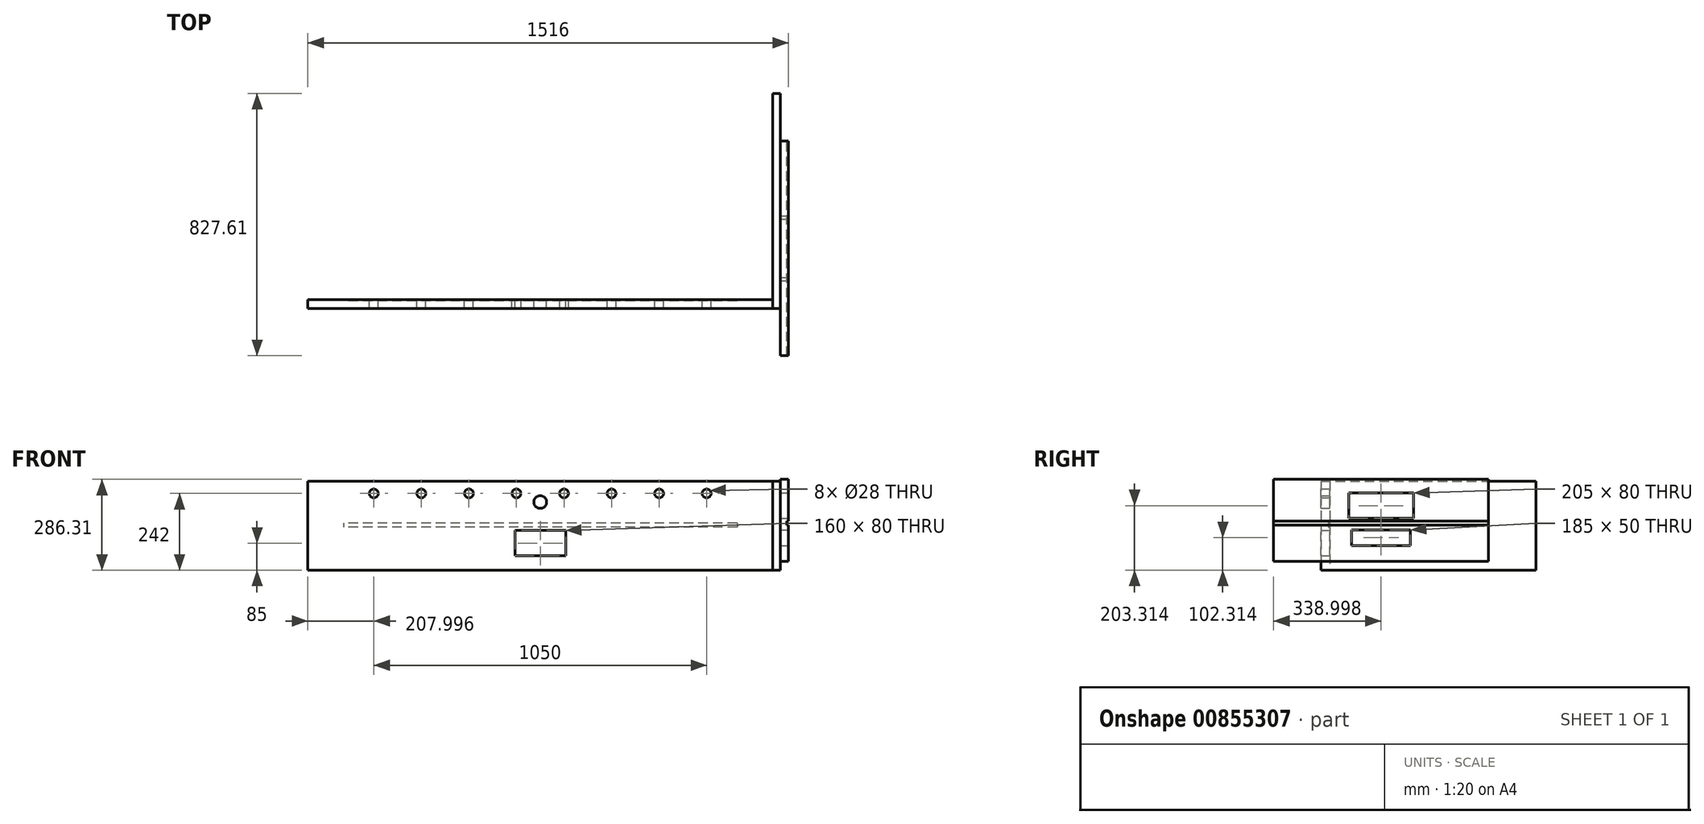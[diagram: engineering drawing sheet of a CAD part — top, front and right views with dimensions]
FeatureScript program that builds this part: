
annotation { "Feature Type Name" : "Feature", "Feature Type Description" : "" }
export const myFeature = defineFeature(function(context is Context, id is Id, definition is map)
    precondition{}
    {
        {
            var Q0;
            Q0=qCreatedBy(makeId("Front.planeOp"),FACE);
            var sketch = newSketch(context, id + "F0", { "sketchPlane" : qUnion([Q0])});
            skLineSegment(sketch, "E0.bottom", {"start": v(-1032.32, -125.07) * mm, "end": v(433.68, -125.07) * mm});
            skLineSegment(sketch, "E0.top", {"start": v(-1032.32, -405.07) * mm, "end": v(433.68, -405.07) * mm});
            skLineSegment(sketch, "E0.left", {"start": v(-1032.32, -125.07) * mm, "end": v(-1032.32, -405.07) * mm});
            skLineSegment(sketch, "E0.right", {"start": v(433.68, -125.07) * mm, "end": v(433.68, -405.07) * mm});
            skCircle(sketch, "E1", {"center": v(-824.32, -163.07) * mm, "radius": 14 * mm});
            skCircle(sketch, "E2", {"center": v(-524.32, -163.07) * mm, "radius": 14 * mm});
            skCircle(sketch, "E3", {"center": v(-374.32, -163.07) * mm, "radius": 14 * mm});
            skCircle(sketch, "E4", {"center": v(-224.32, -163.07) * mm, "radius": 14 * mm});
            skCircle(sketch, "E5", {"center": v(-74.32, -163.07) * mm, "radius": 14 * mm});
            skCircle(sketch, "E6", {"center": v(75.68, -163.07) * mm, "radius": 14 * mm});
            skCircle(sketch, "E7", {"center": v(225.68, -163.07) * mm, "radius": 14 * mm});
            skCircle(sketch, "E8", {"center": v(-674.32, -163.07) * mm, "radius": 14 * mm});
            skCircle(sketch, "E9", {"center": v(-299.32, -190.07) * mm, "radius": 20 * mm});
            skLineSegment(sketch, "E10.bottom", {"start": v(-219.32, -360.07) * mm, "end": v(-379.32, -360.07) * mm});
            skLineSegment(sketch, "E10.top", {"start": v(-219.32, -280.07) * mm, "end": v(-379.32, -280.07) * mm});
            skLineSegment(sketch, "E10.left", {"start": v(-219.32, -360.07) * mm, "end": v(-219.32, -280.07) * mm});
            skLineSegment(sketch, "E10.right", {"start": v(-379.32, -360.07) * mm, "end": v(-379.32, -280.07) * mm});
            skPoint(sketch, "E10.middle", {"position": v(-299.32, -320.07) * mm});
            skSolve(sketch);
        }
        {
            var Q0;
            Q0 = qSketchRegion(id + "F0", true);
            extrude(context, id + "F1", {"entities" : qUnion([Q0]), "depth" : 28 * mm, "offsetDistance" : 25 * mm});
        }
        {
            var Q0;
            Q0=makeQuery(id+"F1.opExtrude","SWEPT_FACE",FACE,{"disambiguationData":[OSD([sQuery(id+"F0.wireOp",EDGE,"E0.right")])]});
            var sketch = newSketch(context, id + "F2", { "sketchPlane" : qUnion([Q0])});
            skLineSegment(sketch, "E11.bottom", {"start": v(-28, -125.07) * mm, "end": v(650, -125.07) * mm});
            skLineSegment(sketch, "E11.top", {"start": v(-28, -405.07) * mm, "end": v(650, -405.07) * mm});
            skLineSegment(sketch, "E11.left", {"start": v(-28, -125.07) * mm, "end": v(-28, -405.07) * mm});
            skLineSegment(sketch, "E11.right", {"start": v(650, -125.07) * mm, "end": v(650, -405.07) * mm});
            skSolve(sketch);
        }
        {
            var Q0;
            Q0 = qSketchRegion(id + "F2", true);
            extrude(context, id + "F3", {"entities" : qUnion([Q0]), "depth" : 25 * mm, "offsetDistance" : 25 * mm});
        }
        {
            var Q0;
            Q0=makeQuery(id+"F1.opExtrude","CAP_FACE",FACE,{"disambiguationData":[OSD([sQuery(id+"F0.wireOp",EDGE,"E0.bottom"),sQuery(id+"F0.wireOp",EDGE,"E0.top"),sQuery(id+"F0.wireOp",EDGE,"E0.left"),sQuery(id+"F0.wireOp",EDGE,"E0.right"),sQuery(id+"F0.wireOp",EDGE,"E1"),sQuery(id+"F0.wireOp",EDGE,"E2"),sQuery(id+"F0.wireOp",EDGE,"E3"),sQuery(id+"F0.wireOp",EDGE,"E4"),sQuery(id+"F0.wireOp",EDGE,"E5"),sQuery(id+"F0.wireOp",EDGE,"E6"),sQuery(id+"F0.wireOp",EDGE,"E7"),sQuery(id+"F0.wireOp",EDGE,"E8"),sQuery(id+"F0.wireOp",EDGE,"E9"),sQuery(id+"F0.wireOp",EDGE,"E10.bottom"),sQuery(id+"F0.wireOp",EDGE,"E10.top"),sQuery(id+"F0.wireOp",EDGE,"E10.left"),sQuery(id+"F0.wireOp",EDGE,"E10.right")])],"isStart":true});
            var sketch = newSketch(context, id + "F4", { "sketchPlane" : qUnion([Q0])});
            skLineSegment(sketch, "E12.bottom", {"start": v(-321.68, -256.07) * mm, "end": v(920.32, -256.07) * mm});
            skLineSegment(sketch, "E12.top", {"start": v(-321.68, -269.07) * mm, "end": v(920.32, -269.07) * mm});
            skLineSegment(sketch, "E12.left", {"start": v(-321.68, -256.07) * mm, "end": v(-321.68, -269.07) * mm});
            skLineSegment(sketch, "E12.right", {"start": v(920.32, -256.07) * mm, "end": v(920.32, -269.07) * mm});
            skSolve(sketch);
        }
        {
            var Q0;
            Q0 = qSketchRegion(id + "F4", true);
            extrude(context, id + "F5", {"entities" : qUnion([Q0]), "operationType" : NewBodyOperationType.REMOVE, "oppositeDirection" : true, "depth" : 5 * mm, "offsetDistance" : 25 * mm});
        }
        {
            var Q0;
            Q0=makeQuery(id+"F3.opExtrude","CAP_FACE",FACE,{"disambiguationData":[OSD([sQuery(id+"F2.wireOp",EDGE,"E11.bottom"),sQuery(id+"F2.wireOp",EDGE,"E11.top"),sQuery(id+"F2.wireOp",EDGE,"E11.left"),sQuery(id+"F2.wireOp",EDGE,"E11.right")])],"isStart":false});
            var sketch = newSketch(context, id + "F6", { "sketchPlane" : qUnion([Q0])});
            skLineSegment(sketch, "E13.bottom", {"start": v(-177.61, -118.76) * mm, "end": v(500.39, -118.76) * mm});
            skLineSegment(sketch, "E13.top", {"start": v(-177.61, -376.76) * mm, "end": v(500.39, -376.76) * mm});
            skLineSegment(sketch, "E13.left", {"start": v(-177.61, -118.76) * mm, "end": v(-177.61, -376.76) * mm});
            skLineSegment(sketch, "E13.right", {"start": v(500.39, -118.76) * mm, "end": v(500.39, -376.76) * mm});
            skSolve(sketch);
        }
        {
            var Q0;
            Q0 = qSketchRegion(id + "F6", true);
            extrude(context, id + "F7", {"entities" : qUnion([Q0]), "depth" : 25 * mm, "offsetDistance" : 25 * mm});
        }
        {
            var Q0;
            Q0=makeQuery(id+"F7.opExtrude","CAP_FACE",FACE,{"disambiguationData":[OSD([sQuery(id+"F6.wireOp",EDGE,"E13.bottom"),sQuery(id+"F6.wireOp",EDGE,"E13.top"),sQuery(id+"F6.wireOp",EDGE,"E13.left"),sQuery(id+"F6.wireOp",EDGE,"E13.right")])],"isStart":false});
            var sketch = newSketch(context, id + "F8", { "sketchPlane" : qUnion([Q0])});
            skLineSegment(sketch, "E14.bottom", {"start": v(263.89, -161.76) * mm, "end": v(58.89, -161.76) * mm});
            skLineSegment(sketch, "E14.top", {"start": v(263.89, -241.76) * mm, "end": v(58.89, -241.76) * mm});
            skLineSegment(sketch, "E14.left", {"start": v(263.89, -161.76) * mm, "end": v(263.89, -241.76) * mm});
            skLineSegment(sketch, "E14.right", {"start": v(58.89, -161.76) * mm, "end": v(58.89, -241.76) * mm});
            skPoint(sketch, "E14.middle", {"position": v(161.39, -201.76) * mm});
            skLineSegment(sketch, "E15.bottom", {"start": v(253.89, -327.76) * mm, "end": v(68.89, -327.76) * mm});
            skLineSegment(sketch, "E15.top", {"start": v(253.89, -277.76) * mm, "end": v(68.89, -277.76) * mm});
            skLineSegment(sketch, "E15.left", {"start": v(253.89, -327.76) * mm, "end": v(253.89, -277.76) * mm});
            skLineSegment(sketch, "E15.right", {"start": v(68.89, -327.76) * mm, "end": v(68.89, -277.76) * mm});
            skPoint(sketch, "E15.middle", {"position": v(161.39, -302.76) * mm});
            skSolve(sketch);
        }
        {
            var Q0;
            Q0=makeQuery(id+"F8.imprint","IMPRINT",FACE,{"disambiguationData":[TD([[makeQuery(id+"F8.imprint","IMPRINT",EDGE,{"derivedFrom":sQuery(id+"F8.wireOp",EDGE,"E14.bottom")}),1.0]])]});
            var Q1;
            Q1=makeQuery(id+"F8.imprint","IMPRINT",FACE,{"disambiguationData":[TD([[makeQuery(id+"F8.imprint","IMPRINT",EDGE,{"derivedFrom":sQuery(id+"F8.wireOp",EDGE,"E15.bottom")}),-1.0]])]});
            var Q2;
            Q2=makeQuery(id+"F7.opExtrude","CAP_FACE",FACE,{"disambiguationData":[OSD([sQuery(id+"F6.wireOp",EDGE,"E13.bottom"),sQuery(id+"F6.wireOp",EDGE,"E13.top"),sQuery(id+"F6.wireOp",EDGE,"E13.left"),sQuery(id+"F6.wireOp",EDGE,"E13.right")])],"isStart":true});
            extrude(context, id + "F9", {"entities" : qUnion([Q0, Q1]), "operationType" : NewBodyOperationType.REMOVE, "endBound" : BoundingType.UP_TO_SURFACE, "oppositeDirection" : true, "depth" : 25 * mm, "endBoundEntityFace" : qUnion([Q2]), "offsetDistance" : 25 * mm});
        }
        {
            var Q0;
            Q0=makeQuery(id+"F7.opExtrude","CAP_FACE",FACE,{"disambiguationData":[OSD([sQuery(id+"F6.wireOp",EDGE,"E13.bottom"),sQuery(id+"F6.wireOp",EDGE,"E13.top"),sQuery(id+"F6.wireOp",EDGE,"E13.left"),sQuery(id+"F6.wireOp",EDGE,"E13.right")])],"isStart":false});
            var sketch = newSketch(context, id + "F10", { "sketchPlane" : qUnion([Q0])});
            skLineSegment(sketch, "E16.bottom", {"start": v(-189.61, -249.76) * mm, "end": v(510.39, -249.76) * mm});
            skLineSegment(sketch, "E16.top", {"start": v(-189.61, -262.76) * mm, "end": v(510.39, -262.76) * mm});
            skLineSegment(sketch, "E16.left", {"start": v(-189.61, -249.76) * mm, "end": v(-189.61, -262.76) * mm});
            skLineSegment(sketch, "E16.right", {"start": v(510.39, -249.76) * mm, "end": v(510.39, -262.76) * mm});
            skSolve(sketch);
        }
        {
            var Q0;
            {var subQ0=sQuery(id+"F10.wireOp",EDGE,"E16.bottom");var subQ1=makeQuery(id+"F7.opExtrude","CAP_EDGE",EDGE,{"disambiguationData":[OSD([sQuery(id+"F6.wireOp",EDGE,"E13.left")])],"isStart":false});var subQ2=makeQuery(id+"F10.imprint","INTERSECT",VERTEX,{"derivedFrom":[subQ1,subQ0]});Q0=makeQuery(id+"F10.imprint","IMPRINT",FACE,{"disambiguationData":[TD([[makeQuery(id+"F10.imprint","IMPRINT",EDGE,{"disambiguationData":[TD([[subQ2,-1.0]])],"derivedFrom":subQ0}),-1.0]])]});}
            extrude(context, id + "F11", {"entities" : qUnion([Q0]), "operationType" : NewBodyOperationType.REMOVE, "oppositeDirection" : true, "depth" : 5 * mm, "offsetDistance" : 25 * mm});
        }
    });
